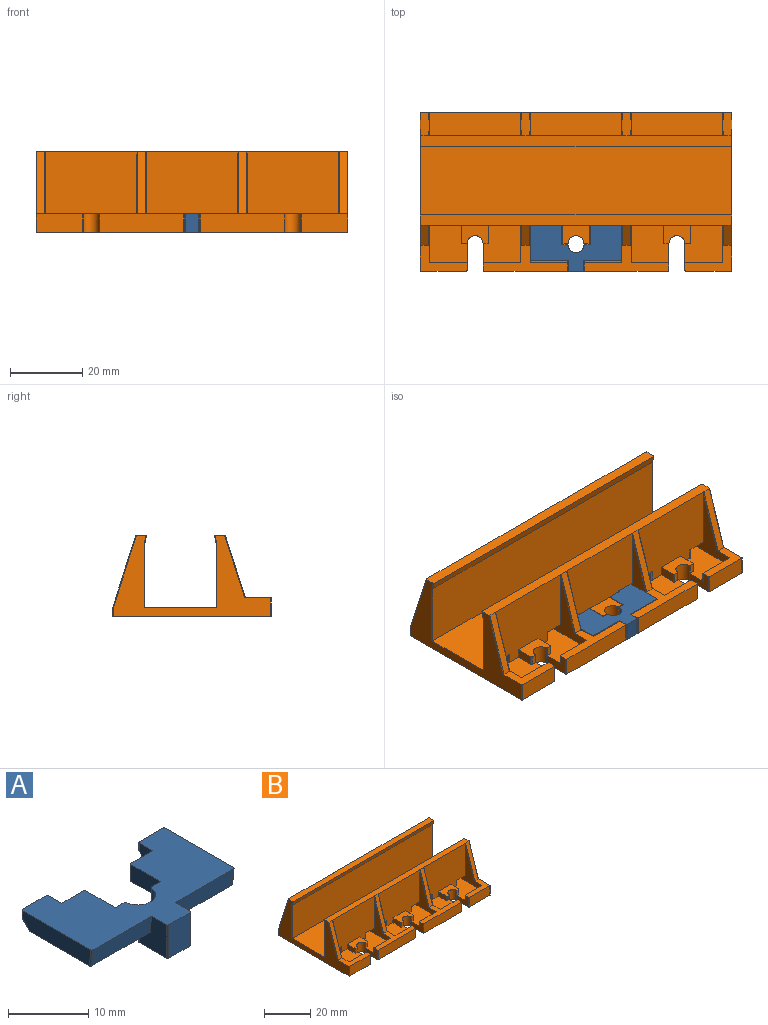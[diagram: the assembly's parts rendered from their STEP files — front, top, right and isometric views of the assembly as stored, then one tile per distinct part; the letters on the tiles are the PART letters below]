
ASSEMBLY  parts=2 mates=1
PART A: 44 faces, bbox 25.1x15.2x5.1 mm
  f0: plane 5.23x4.14mm, normal (0,0,-1), area 21.5mm2, adj f18,f19,f20,f21,f22,f23,f34,f35
  f1: plane 2.54x1.55mm, normal (0,1,0), area 3.9mm2, adj f2,f5,f15,f36
  f2: plane 11.78x10.91mm, normal (0,0,-1), area 97mm2, adj f1,f3,f7,f8,f14,f15,f18,f21
  f3: plane 10.28x2.54mm, normal (0,-1,-0.09), area 26.2mm2, adj f2,f5,f18,f43
  f4: plane 3.81x2.54mm, normal (0,1,0), area 9.7mm2, adj f5,f6,f11,f41
  f5: plane 25.1x15.25mm, normal (0,0,1), area 231.8mm2, adj f1,f3,f4,f7,f8,f9,f10,f11
  f6: plane 11.78x10.91mm, normal (0,0,-1), area 97mm2, adj f4,f9,f10,f11,f16,f17,f19,f21
  f7: plane 3.81x2.54mm, normal (0,1,0), area 9.7mm2, adj f2,f5,f14,f40
  f8: plane 11.99x2.54mm, normal (1,0,0), area 29.3mm2, adj f2,f5,f28,f29,f43
  f9: plane 11.99x2.54mm, normal (-1,0,0), area 29.3mm2, adj f5,f6,f30,f31,f42
  f10: plane 10.28x2.54mm, normal (0,-1,-0.09), area 26.2mm2, adj f5,f6,f19,f42
  f11: plane 2.54x2.34mm, normal (1,0,0), area 5mm2, adj f4,f5,f6,f32,f33
  f12: plane 4.17x1.27mm, normal (0,1,0), area 5.3mm2, adj f5,f24,f30,f32
  f13: plane 4.17x1.27mm, normal (0,1,0), area 5.3mm2, adj f5,f25,f26,f28
  f14: plane 2.54x2.34mm, normal (-1,0,0), area 5mm2, adj f2,f5,f7,f26,f27
  f15: plane 5.19x2.54mm, normal (-1,0,0), area 13.2mm2, adj f1,f2,f5,f40
  f16: plane 5.19x2.54mm, normal (1,0,0), area 13.2mm2, adj f5,f6,f17,f41
  f17: plane 2.54x1.55mm, normal (0,1,0), area 3.9mm2, adj f5,f6,f16,f37
  f18: plane 5.08x4.83mm, normal (1,0,0), area 19.3mm2, adj f0,f2,f3,f5,f34,f39
  f19: plane 5.08x4.83mm, normal (-1,0,0), area 19.3mm2, adj f0,f5,f6,f10,f35,f38
  f20: plane 5.08x3.74mm, normal (0,-1,0), area 19mm2, adj f0,f5,f38,f39
  f21: cylinder r=2.22mm len=5.08mm, axis (0,0,1), area 20.8mm2, adj f0,f2,f5,f6,f22,f23,f36,f37
  f22: plane 2.54x1.09mm, normal (0,1,0), area 2.8mm2, adj f0,f6,f21,f35
  f23: plane 2.54x1.09mm, normal (0,1,0), area 2.8mm2, adj f0,f2,f21,f34
  f24: plane 4.17x1.27mm, normal (0,0.71,-0.71), area 7.5mm2, adj f6,f12,f31,f33
  f25: plane 4.17x1.27mm, normal (0,0.71,-0.71), area 7.5mm2, adj f2,f13,f27,f29
  f26: cylinder r=0.2mm len=1.27mm, axis (0,0,-1), area 0.4mm2, adj f5,f13,f14,f27
  f27: cylinder r=0.2mm len=1.55mm, axis (0,0.71,0.71), area 0.6mm2, adj f2,f14,f25,f26
  f28: cylinder r=0.2mm len=1.27mm, axis (0,0,-1), area 0.4mm2, adj f5,f8,f13,f29
  f29: cylinder r=0.2mm len=1.55mm, axis (0,-0.71,-0.71), area 0.6mm2, adj f2,f8,f25,f28
  f30: cylinder r=0.2mm len=1.27mm, axis (0,0,1), area 0.4mm2, adj f5,f9,f12,f31
  f31: cylinder r=0.2mm len=1.55mm, axis (0,-0.71,-0.71), area 0.6mm2, adj f6,f9,f24,f30
  f32: cylinder r=0.2mm len=1.27mm, axis (0,0,1), area 0.4mm2, adj f5,f11,f12,f33
  f33: cylinder r=0.2mm len=1.55mm, axis (0,0.71,0.71), area 0.6mm2, adj f6,f11,f24,f32
  f34: cylinder r=0.2mm len=2.54mm, axis (0,0,1), area 0.8mm2, adj f0,f2,f18,f23
  f35: cylinder r=0.2mm len=2.54mm, axis (0,0,-1), area 0.8mm2, adj f0,f6,f19,f22
  f36: cylinder r=0.2mm len=2.54mm, axis (0,0,1), area 0.8mm2, adj f1,f2,f5,f21
  f37: cylinder r=0.2mm len=2.54mm, axis (0,0,1), area 0.8mm2, adj f5,f6,f17,f21
  f38: cylinder r=0.2mm len=5.08mm, axis (0,0,1), area 1.6mm2, adj f0,f5,f19,f20
  f39: cylinder r=0.2mm len=5.08mm, axis (0,0,-1), area 1.6mm2, adj f0,f5,f18,f20
  f40: cylinder r=0.2mm len=2.54mm, axis (0,0,-1), area 0.8mm2, adj f2,f5,f7,f15
  f41: cylinder r=0.2mm len=2.54mm, axis (0,0,1), area 0.8mm2, adj f4,f5,f6,f16
  f42: cylinder r=0.2mm len=2.58mm, axis (0,-0.09,1), area 0.8mm2, adj f5,f6,f9,f10
  f43: cylinder r=0.2mm len=2.58mm, axis (0,0.09,-1), area 0.8mm2, adj f2,f3,f5,f8
PART B: 160 faces, bbox 86.4x43.9x22.4 mm
  f0: plane 10.28x2.54mm, normal (0,1,0), area 26.1mm2, adj f3,f21,f57,f133
  f1: plane 10.28x2.54mm, normal (0,1,0), area 26.1mm2, adj f3,f20,f51,f131
  f2: plane 10.28x2.54mm, normal (0,1,0), area 26.1mm2, adj f3,f19,f46,f129
  f3: plane 86.36x32.86mm, normal (0,0,1), area 2374.7mm2, adj f0,f1,f2,f4,f5,f6,f7,f17
  f4: plane 25.8x19.76mm, normal (0,-1,0), area 453.1mm2, adj f3,f23,f57,f62,f65,f67,f85,f86
  f5: plane 25.8x19.76mm, normal (0,-1,0), area 453.1mm2, adj f3,f23,f51,f58,f63,f71,f80,f81
  f6: plane 25.8x19.76mm, normal (0,-1,0), area 453.1mm2, adj f3,f23,f46,f52,f69,f74,f76,f77
  f7: plane 85.96x17.64mm, normal (0,1,0), area 1424mm2, adj f3,f22,f63,f65,f67,f69,f71,f74
  f8: plane 25.8x6.35mm, normal (0,0,1), area 161.3mm2, adj f9,f28,f54,f60,f146,f150
  f9: plane 25.8x19.76mm, normal (0,1,0), area 502mm2, adj f8,f29,f54,f60,f146,f150
  f10: plane 25.8x6.35mm, normal (0,0,1), area 161.3mm2, adj f11,f28,f48,f55,f149,f152
  f11: plane 25.8x19.76mm, normal (0,1,0), area 502mm2, adj f10,f29,f48,f55,f149,f152
  f12: plane 25.8x6.35mm, normal (0,0,1), area 161.3mm2, adj f13,f28,f44,f49,f151,f155
  f13: plane 25.8x19.76mm, normal (0,1,0), area 502mm2, adj f12,f29,f44,f49,f151,f155
  f14: plane 23.1x5.08mm, normal (0,-1,0), area 117.3mm2, adj f20,f27,f137,f138
  f15: plane 23.1x5.08mm, normal (0,-1,0), area 117.3mm2, adj f21,f27,f134,f136
  f16: plane 12.62x5.08mm, normal (0,-1,0), area 64.1mm2, adj f25,f27,f135,f145
  f17: plane 10.28x2.54mm, normal (0,1,0), area 26.1mm2, adj f3,f20,f52,f128
  f18: plane 10.28x2.54mm, normal (0,1,0), area 26.1mm2, adj f3,f21,f58,f130
  f19: plane 13.02x7.38mm, normal (0,0,1), area 44.8mm2, adj f2,f26,f33,f42,f45,f46,f126,f127
  f20: plane 23.5x7.38mm, normal (0,0,1), area 71.4mm2, adj f1,f14,f17,f39,f40,f50,f51,f52
  f21: plane 23.5x7.38mm, normal (0,0,1), area 71.4mm2, adj f0,f15,f18,f36,f37,f56,f57,f58
  f22: plane 85.96x2.13mm, normal (0,0.97,-0.23), area 187.9mm2, adj f7,f23,f140,f143
  f23: plane 86.36x3.05mm, normal (0,0,1), area 263.2mm2, adj f4,f5,f6,f22,f32,f33,f45,f50
  f24: plane 10.28x2.54mm, normal (0,1,0), area 26.1mm2, adj f3,f25,f62,f132
  f25: plane 13.02x7.38mm, normal (0,0,1), area 44.8mm2, adj f16,f24,f32,f34,f61,f62,f120,f121
  f26: plane 12.62x5.08mm, normal (0,-1,0), area 64.1mm2, adj f19,f27,f139,f142
  f27: plane 86.36x43.89mm, normal (0,0,-1), area 3665.5mm2, adj f14,f15,f16,f26,f28,f32,f33,f34
  f28: plane 85.96x2.54mm, normal (0,1,0), area 218.3mm2, adj f8,f10,f12,f27,f43,f47,f53,f59
  f29: plane 86.36x3.05mm, normal (0,0,1), area 263.2mm2, adj f9,f11,f13,f30,f32,f33,f43,f47
  f30: plane 85.96x2.13mm, normal (0,-0.97,-0.23), area 187.9mm2, adj f29,f31,f156,f158
  f31: plane 85.96x17.64mm, normal (0,-1,0), area 1515.9mm2, adj f3,f30,f157,f159
  f32: plane 43.49x22.3mm, normal (1,0,0), area 338.4mm2, adj f3,f23,f25,f27,f29,f121,f143,f144
  f33: plane 43.49x22.3mm, normal (-1,0,0), area 338.4mm2, adj f3,f19,f23,f27,f29,f126,f140,f141
  f34: plane 7.42x5.08mm, normal (-1,0,0), area 24.3mm2, adj f3,f25,f27,f35,f132,f135
  f35: cylinder r=2.22mm len=5.08mm, axis (0,0,-1), area 34.5mm2, adj f3,f27,f34,f36,f89,f91,f92
  f36: plane 7.42x5.08mm, normal (1,0,0), area 24.3mm2, adj f3,f21,f27,f35,f133,f134
  f37: plane 7.42x5.08mm, normal (-1,0,0), area 24.3mm2, adj f3,f21,f27,f38,f130,f136
  f38: cylinder r=2.22mm len=5.08mm, axis (0,0,-1), area 34.5mm2, adj f3,f27,f37,f39,f84,f95,f96
  f39: plane 7.42x5.08mm, normal (1,0,0), area 24.3mm2, adj f3,f20,f27,f38,f131,f137
  f40: plane 7.42x5.08mm, normal (-1,0,0), area 24.3mm2, adj f3,f20,f27,f41,f128,f138
  f41: cylinder r=2.22mm len=5.08mm, axis (0,0,-1), area 34.5mm2, adj f3,f27,f40,f42,f79,f98,f101
  f42: plane 7.42x5.08mm, normal (1,0,0), area 24.3mm2, adj f3,f19,f27,f41,f129,f139
  f43: plane 19.76x6.35mm, normal (0,0.95,0.31), area 44.4mm2, adj f28,f29,f154,f155
  f44: plane 19.11x6.14mm, normal (1,0,0), area 58.7mm2, adj f12,f13,f155
  f45: plane 17.22x5.53mm, normal (0,-0.95,0.31), area 38.7mm2, adj f19,f23,f126,f127
  f46: plane 19.11x12.5mm, normal (1,0,0), area 76.4mm2, adj f2,f3,f6,f19,f74,f117,f127
  f47: plane 19.76x6.35mm, normal (0,0.95,0.31), area 44.4mm2, adj f28,f29,f151,f152
  f48: plane 19.11x6.14mm, normal (1,0,0), area 58.7mm2, adj f10,f11,f152
  f49: plane 19.11x6.14mm, normal (-1,0,0), area 58.7mm2, adj f12,f13,f151
  f50: plane 17.22x5.53mm, normal (0,-0.95,0.31), area 38.7mm2, adj f20,f23,f124,f125
  f51: plane 19.11x12.5mm, normal (1,0,0), area 76.4mm2, adj f1,f3,f5,f20,f71,f102,f125
  f52: plane 19.11x12.5mm, normal (-1,0,0), area 76.4mm2, adj f3,f6,f17,f20,f69,f115,f124
  f53: plane 19.76x6.35mm, normal (0,0.95,0.31), area 44.4mm2, adj f28,f29,f149,f150
  f54: plane 19.11x6.14mm, normal (1,0,0), area 58.7mm2, adj f8,f9,f150
  f55: plane 19.11x6.14mm, normal (-1,0,0), area 58.7mm2, adj f10,f11,f149
  f56: plane 17.22x5.53mm, normal (0,-0.95,0.31), area 38.7mm2, adj f21,f23,f122,f123
  f57: plane 19.11x12.5mm, normal (1,0,0), area 76.4mm2, adj f0,f3,f4,f21,f65,f108,f123
  f58: plane 19.11x12.5mm, normal (-1,0,0), area 76.4mm2, adj f3,f5,f18,f21,f63,f106,f122
  f59: plane 19.76x6.35mm, normal (0,0.95,0.31), area 44.4mm2, adj f28,f29,f146,f148
  f60: plane 19.11x6.14mm, normal (-1,0,0), area 58.7mm2, adj f8,f9,f146
  f61: plane 17.22x5.53mm, normal (0,-0.95,0.31), area 38.7mm2, adj f23,f25,f120,f121
  f62: plane 19.11x12.5mm, normal (-1,0,0), area 76.4mm2, adj f3,f4,f24,f25,f67,f112,f120
  f63: plane 5.48x2.54mm, normal (0,0,-1), area 12.9mm2, adj f5,f7,f58,f64,f105,f106,f107
  f64: plane 2.79x2.14mm, normal (1,0,0), area 6mm2, adj f3,f63,f105,f107
  f65: plane 5.48x2.54mm, normal (0,0,-1), area 12.9mm2, adj f4,f7,f57,f66,f108,f109,f110
  f66: plane 2.79x2.14mm, normal (-1,0,0), area 6mm2, adj f3,f65,f109,f110
  f67: plane 5.48x2.54mm, normal (0,0,-1), area 12.9mm2, adj f4,f7,f62,f68,f111,f112,f113
  f68: plane 2.79x2.14mm, normal (1,0,0), area 6mm2, adj f3,f67,f111,f113
  f69: plane 5.48x2.54mm, normal (0,0,-1), area 12.9mm2, adj f6,f7,f52,f70,f114,f115,f116
  f70: plane 2.79x2.14mm, normal (1,0,0), area 6mm2, adj f3,f69,f114,f116
  f71: plane 5.48x2.54mm, normal (0,0,-1), area 12.9mm2, adj f5,f7,f51,f72,f102,f103,f104
  f72: plane 2.79x2.14mm, normal (-1,0,0), area 6mm2, adj f3,f71,f103,f104
  f73: plane 2.79x2.14mm, normal (-1,0,0), area 6mm2, adj f3,f74,f118,f119
  f74: plane 5.48x2.54mm, normal (0,0,-1), area 12.9mm2, adj f6,f7,f46,f73,f117,f118,f119
  f75: plane 2.54x1.2mm, normal (0,-1,0), area 3mm2, adj f3,f79,f100,f101
  f76: plane 4.88x2.54mm, normal (1,0,0), area 12.4mm2, adj f3,f6,f79,f100
  f77: plane 4.88x2.54mm, normal (-1,0,0), area 12.4mm2, adj f3,f6,f79,f99
  f78: plane 2.54x1.2mm, normal (0,-1,0), area 3mm2, adj f3,f79,f98,f99
  f79: plane 7.62x5.08mm, normal (0,0,1), area 30.9mm2, adj f6,f41,f75,f76,f77,f78,f98,f99
  f80: plane 4.88x2.54mm, normal (1,0,0), area 12.4mm2, adj f3,f5,f84,f97
  f81: plane 4.88x2.54mm, normal (-1,0,0), area 12.4mm2, adj f3,f5,f84,f94
  f82: plane 2.54x1.2mm, normal (0,-1,0), area 3mm2, adj f3,f84,f94,f95
  f83: plane 2.54x1.2mm, normal (0,-1,0), area 3mm2, adj f3,f84,f96,f97
  f84: plane 7.62x5.08mm, normal (0,0,1), area 30.9mm2, adj f5,f38,f80,f81,f82,f83,f94,f95
  f85: plane 4.88x2.54mm, normal (1,0,0), area 12.4mm2, adj f3,f4,f89,f90
  f86: plane 4.88x2.54mm, normal (-1,0,0), area 12.4mm2, adj f3,f4,f89,f93
  f87: plane 2.54x1.2mm, normal (0,-1,0), area 3mm2, adj f3,f89,f92,f93
  f88: plane 2.54x1.2mm, normal (0,-1,0), area 3mm2, adj f3,f89,f90,f91
  f89: plane 7.62x5.08mm, normal (0,0,1), area 30.9mm2, adj f4,f35,f85,f86,f87,f88,f90,f91
  f90: cylinder r=0.2mm len=2.54mm, axis (0,0,1), area 0.8mm2, adj f3,f85,f88,f89
  f91: cylinder r=0.2mm len=2.54mm, axis (0,0,-1), area 0.8mm2, adj f3,f35,f88,f89
  f92: cylinder r=0.2mm len=2.54mm, axis (0,0,-1), area 0.8mm2, adj f3,f35,f87,f89
  f93: cylinder r=0.2mm len=2.54mm, axis (0,0,-1), area 0.8mm2, adj f3,f86,f87,f89
  f94: cylinder r=0.2mm len=2.54mm, axis (0,0,-1), area 0.8mm2, adj f3,f81,f82,f84
  f95: cylinder r=0.2mm len=2.54mm, axis (0,0,-1), area 0.8mm2, adj f3,f38,f82,f84
  f96: cylinder r=0.2mm len=2.54mm, axis (0,0,-1), area 0.8mm2, adj f3,f38,f83,f84
  f97: cylinder r=0.2mm len=2.54mm, axis (0,0,1), area 0.8mm2, adj f3,f80,f83,f84
  f98: cylinder r=0.2mm len=2.54mm, axis (0,0,-1), area 0.8mm2, adj f3,f41,f78,f79
  f99: cylinder r=0.2mm len=2.54mm, axis (0,0,-1), area 0.8mm2, adj f3,f77,f78,f79
  f100: cylinder r=0.2mm len=2.54mm, axis (0,0,1), area 0.8mm2, adj f3,f75,f76,f79
  f101: cylinder r=0.2mm len=2.54mm, axis (0,0,-1), area 0.8mm2, adj f3,f41,f75,f79
  f102: cylinder r=0.2mm len=2.79mm, axis (0,0,-1), area 0.9mm2, adj f3,f7,f51,f71
  f103: cylinder r=0.2mm len=2.79mm, axis (0,0,-1), area 0.9mm2, adj f3,f7,f71,f72
  f104: cylinder r=0.2mm len=2.79mm, axis (0,0,-1), area 0.9mm2, adj f3,f5,f71,f72
  f105: cylinder r=0.2mm len=2.79mm, axis (0,0,1), area 0.9mm2, adj f3,f7,f63,f64
  f106: cylinder r=0.2mm len=2.79mm, axis (0,0,1), area 0.9mm2, adj f3,f7,f58,f63
  f107: cylinder r=0.2mm len=2.79mm, axis (0,0,1), area 0.9mm2, adj f3,f5,f63,f64
  f108: cylinder r=0.2mm len=2.79mm, axis (0,0,1), area 0.9mm2, adj f3,f7,f57,f65
  f109: cylinder r=0.2mm len=2.79mm, axis (0,0,-1), area 0.9mm2, adj f3,f7,f65,f66
  f110: cylinder r=0.2mm len=2.79mm, axis (0,0,-1), area 0.9mm2, adj f3,f4,f65,f66
  f111: cylinder r=0.2mm len=2.79mm, axis (0,0,1), area 0.9mm2, adj f3,f7,f67,f68
  f112: cylinder r=0.2mm len=2.79mm, axis (0,0,-1), area 0.9mm2, adj f3,f7,f62,f67
  f113: cylinder r=0.2mm len=2.79mm, axis (0,0,1), area 0.9mm2, adj f3,f4,f67,f68
  f114: cylinder r=0.2mm len=2.79mm, axis (0,0,1), area 0.9mm2, adj f3,f7,f69,f70
  f115: cylinder r=0.2mm len=2.79mm, axis (0,0,-1), area 0.9mm2, adj f3,f7,f52,f69
  f116: cylinder r=0.2mm len=2.79mm, axis (0,0,1), area 0.9mm2, adj f3,f6,f69,f70
  f117: cylinder r=0.2mm len=2.79mm, axis (0,0,1), area 0.9mm2, adj f3,f7,f46,f74
  f118: cylinder r=0.2mm len=2.79mm, axis (0,0,-1), area 0.9mm2, adj f3,f7,f73,f74
  f119: cylinder r=0.2mm len=2.79mm, axis (0,0,-1), area 0.9mm2, adj f3,f6,f73,f74
  f120: cylinder r=0.2mm len=17.28mm, axis (0,0.31,0.95), area 5.6mm2, adj f4,f25,f61,f62
  f121: cylinder r=0.2mm len=17.34mm, axis (0,0.31,0.95), area 5.7mm2, adj f23,f25,f32,f61
  f122: cylinder r=0.2mm len=17.28mm, axis (0,0.31,0.95), area 5.6mm2, adj f5,f21,f56,f58
  f123: cylinder r=0.2mm len=17.28mm, axis (0,-0.31,-0.95), area 5.6mm2, adj f4,f21,f56,f57
  f124: cylinder r=0.2mm len=17.28mm, axis (0,0.31,0.95), area 5.6mm2, adj f6,f20,f50,f52
  f125: cylinder r=0.2mm len=17.28mm, axis (0,-0.31,-0.95), area 5.6mm2, adj f5,f20,f50,f51
  f126: cylinder r=0.2mm len=17.34mm, axis (0,-0.31,-0.95), area 5.7mm2, adj f19,f23,f33,f45
  f127: cylinder r=0.2mm len=17.28mm, axis (0,-0.31,-0.95), area 5.6mm2, adj f6,f19,f45,f46
  f128: cylinder r=0.2mm len=2.54mm, axis (0,0,1), area 0.8mm2, adj f3,f17,f20,f40
  f129: cylinder r=0.2mm len=2.54mm, axis (0,0,-1), area 0.8mm2, adj f2,f3,f19,f42
  f130: cylinder r=0.2mm len=2.54mm, axis (0,0,1), area 0.8mm2, adj f3,f18,f21,f37
  f131: cylinder r=0.2mm len=2.54mm, axis (0,0,-1), area 0.8mm2, adj f1,f3,f20,f39
  f132: cylinder r=0.2mm len=2.54mm, axis (0,0,1), area 0.8mm2, adj f3,f24,f25,f34
  f133: cylinder r=0.2mm len=2.54mm, axis (0,0,-1), area 0.8mm2, adj f0,f3,f21,f36
  f134: cylinder r=0.2mm len=5.08mm, axis (0,0,-1), area 1.6mm2, adj f15,f21,f27,f36
  f135: cylinder r=0.2mm len=5.08mm, axis (0,0,1), area 1.6mm2, adj f16,f25,f27,f34
  f136: cylinder r=0.2mm len=5.08mm, axis (0,0,1), area 1.6mm2, adj f15,f21,f27,f37
  f137: cylinder r=0.2mm len=5.08mm, axis (0,0,-1), area 1.6mm2, adj f14,f20,f27,f39
  f138: cylinder r=0.2mm len=5.08mm, axis (0,0,1), area 1.6mm2, adj f14,f20,f27,f40
  f139: cylinder r=0.2mm len=5.08mm, axis (0,0,-1), area 1.6mm2, adj f19,f26,f27,f42
  f140: cylinder r=0.2mm len=2.2mm, axis (0,0.23,0.97), area 0.7mm2, adj f22,f23,f33,f141
  f141: cylinder r=0.2mm len=17.66mm, axis (0,0,1), area 5.5mm2, adj f3,f7,f33,f140
  f142: cylinder r=0.2mm len=5.08mm, axis (0,0,-1), area 1.6mm2, adj f19,f26,f27,f33
  f143: cylinder r=0.2mm len=2.2mm, axis (0,-0.23,-0.97), area 0.7mm2, adj f22,f23,f32,f144
  f144: cylinder r=0.2mm len=17.66mm, axis (0,0,-1), area 5.5mm2, adj f3,f7,f32,f143
  f145: cylinder r=0.2mm len=5.08mm, axis (0,0,1), area 1.6mm2, adj f16,f25,f27,f32
  f146: cylinder r=0.2mm len=19.82mm, axis (0,0.31,-0.95), area 6.4mm2, adj f8,f9,f59,f60
  f147: cylinder r=0.2mm len=2.54mm, axis (0,0,-1), area 0.8mm2, adj f27,f28,f32,f148
  f148: cylinder r=0.2mm len=19.88mm, axis (0,0.31,-0.95), area 6.5mm2, adj f29,f32,f59,f147
  f149: cylinder r=0.2mm len=19.82mm, axis (0,0.31,-0.95), area 6.4mm2, adj f10,f11,f53,f55
  f150: cylinder r=0.2mm len=19.82mm, axis (0,-0.31,0.95), area 6.4mm2, adj f8,f9,f53,f54
  f151: cylinder r=0.2mm len=19.82mm, axis (0,0.31,-0.95), area 6.4mm2, adj f12,f13,f47,f49
  f152: cylinder r=0.2mm len=19.82mm, axis (0,-0.31,0.95), area 6.4mm2, adj f10,f11,f47,f48
  f153: cylinder r=0.2mm len=2.54mm, axis (0,0,1), area 0.8mm2, adj f27,f28,f33,f154
  f154: cylinder r=0.2mm len=19.88mm, axis (0,-0.31,0.95), area 6.5mm2, adj f29,f33,f43,f153
  f155: cylinder r=0.2mm len=19.82mm, axis (0,-0.31,0.95), area 6.4mm2, adj f12,f13,f43,f44
  f156: cylinder r=0.2mm len=2.2mm, axis (0,0.23,-0.97), area 0.7mm2, adj f29,f30,f33,f157
  f157: cylinder r=0.2mm len=17.66mm, axis (0,0,-1), area 5.5mm2, adj f3,f31,f33,f156
  f158: cylinder r=0.2mm len=2.2mm, axis (0,-0.23,0.97), area 0.7mm2, adj f29,f30,f32,f159
  f159: cylinder r=0.2mm len=17.66mm, axis (0,0,1), area 5.5mm2, adj f3,f31,f32,f158
PLACE A t=(0,-8.89,-2.54)mm
PLACE B t=(0,-3.96,-5.08)mm
MATE planar B.f5 <-> A.f4  axis (0,-1,0) through (0,-3.96,8.26)mm
